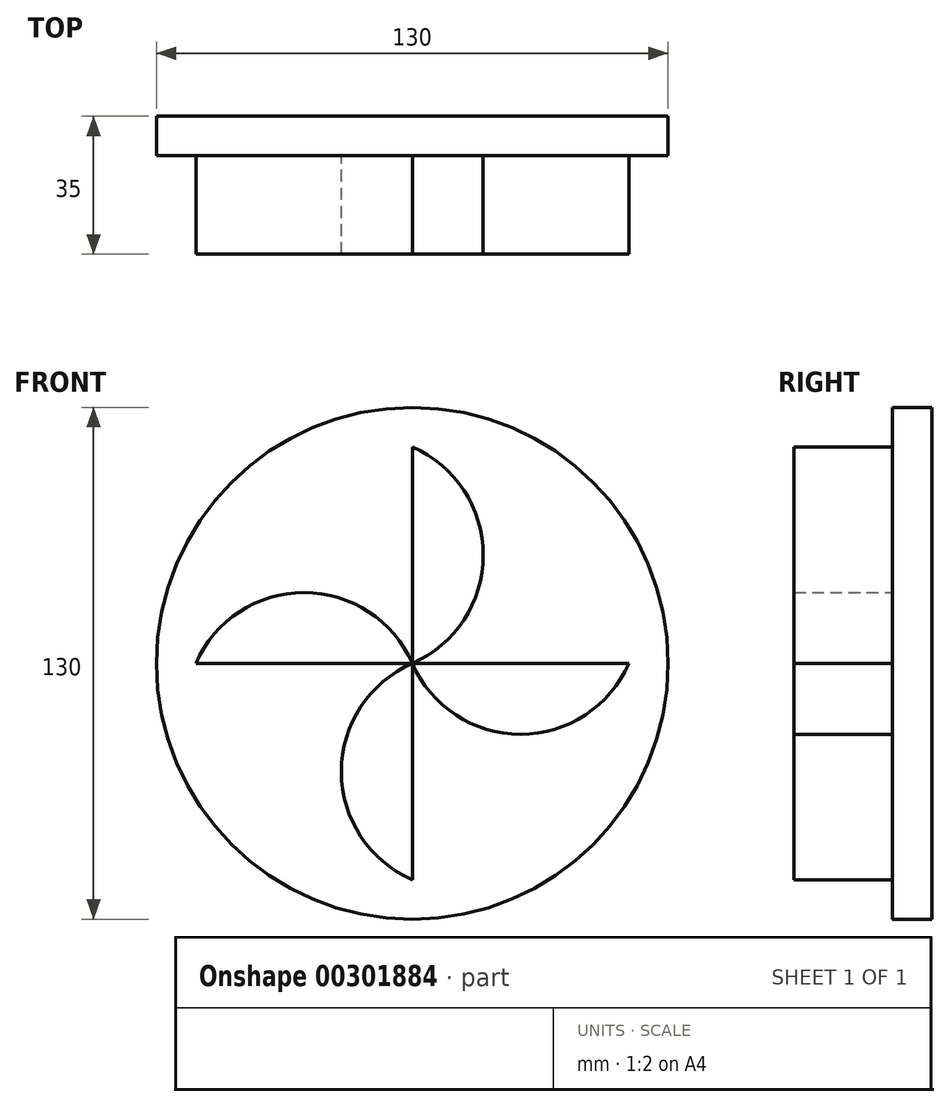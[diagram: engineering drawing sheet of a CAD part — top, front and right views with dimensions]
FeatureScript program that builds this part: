
annotation { "Feature Type Name" : "Feature", "Feature Type Description" : "" }
export const myFeature = defineFeature(function(context is Context, id is Id, definition is map)
    precondition{}
    {
        {
            var Q0;
            Q0=qCreatedBy(makeId("Front.planeOp"),FACE);
            var sketch = newSketch(context, id + "F0", { "sketchPlane" : qUnion([Q0])});
            skCircle(sketch, "E0", {"center": v(0, 0) * mm, "radius": 65 * mm});
            skSolve(sketch);
        }
        {
            var Q0;
            Q0 = qSketchRegion(id + "F0", true);
            extrude(context, id + "F1", {"entities" : qUnion([Q0]), "depth" : 10 * mm});
        }
        {
            var Q0;
            Q0=makeQuery(id+"F1.opExtrude","CAP_FACE",FACE,{"disambiguationData":[OSD([sQuery(id+"F0.wireOp",EDGE,"E0")])],"isStart":false});
            var sketch = newSketch(context, id + "F2", { "sketchPlane" : qUnion([Q0])});
            skArc(sketch, "E1", {"start": v(0, 0) * mm, "mid": v(18.01, 27.5) * mm, "end": v(0, 55) * mm});
            skArc(sketch, "E2", {"start": v(0, 0) * mm, "mid": v(27.5, -18.01) * mm, "end": v(55, 0) * mm});
            skArc(sketch, "E3", {"start": v(0, 0) * mm, "mid": v(-18.01, -27.5) * mm, "end": v(0, -55) * mm});
            skArc(sketch, "E4", {"start": v(0, 0) * mm, "mid": v(-27.5, 18.01) * mm, "end": v(-55, 0) * mm});
            skLineSegment(sketch, "E5", {"start": v(0, 55) * mm, "end": v(0, 0) * mm});
            skLineSegment(sketch, "E6", {"start": v(-55, 0) * mm, "end": v(0, 0) * mm});
            skLineSegment(sketch, "E7", {"start": v(0, -55) * mm, "end": v(0, 0) * mm});
            skLineSegment(sketch, "E8", {"start": v(0, 0) * mm, "end": v(55, 0) * mm});
            skSolve(sketch);
        }
        {
            var Q0;
            Q0 = qSketchRegion(id + "F2", true);
            extrude(context, id + "F3", {"entities" : qUnion([Q0]), "depth" : 25 * mm});
        }
    });
